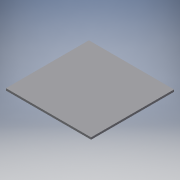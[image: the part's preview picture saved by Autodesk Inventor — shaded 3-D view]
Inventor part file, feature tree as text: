
AUTODESK INVENTOR PART (.ipt)
format: ipt  version: 2018.2 (Build 222227000, 227)  size: 93,184 bytes
history: native  units: in
note: dims shown in document units (in); Inventor stores cm internally (conversion verified against a paired STEP export)
features: extrude x1, sketch x1
ambient origin geometry x8: Origin, YZ Plane, XZ Plane, XY Plane, X Axis, Y Axis, Z Axis, Center Point
bodies: Solid1 (feature_tree)
feature tree (2):
  extrude  "Extrusion1"  Depth=0.75in
  sketch  "Sketch1"  dims[d0=30.0in d1=0.75in d2=30.898in d3=0.0in]
